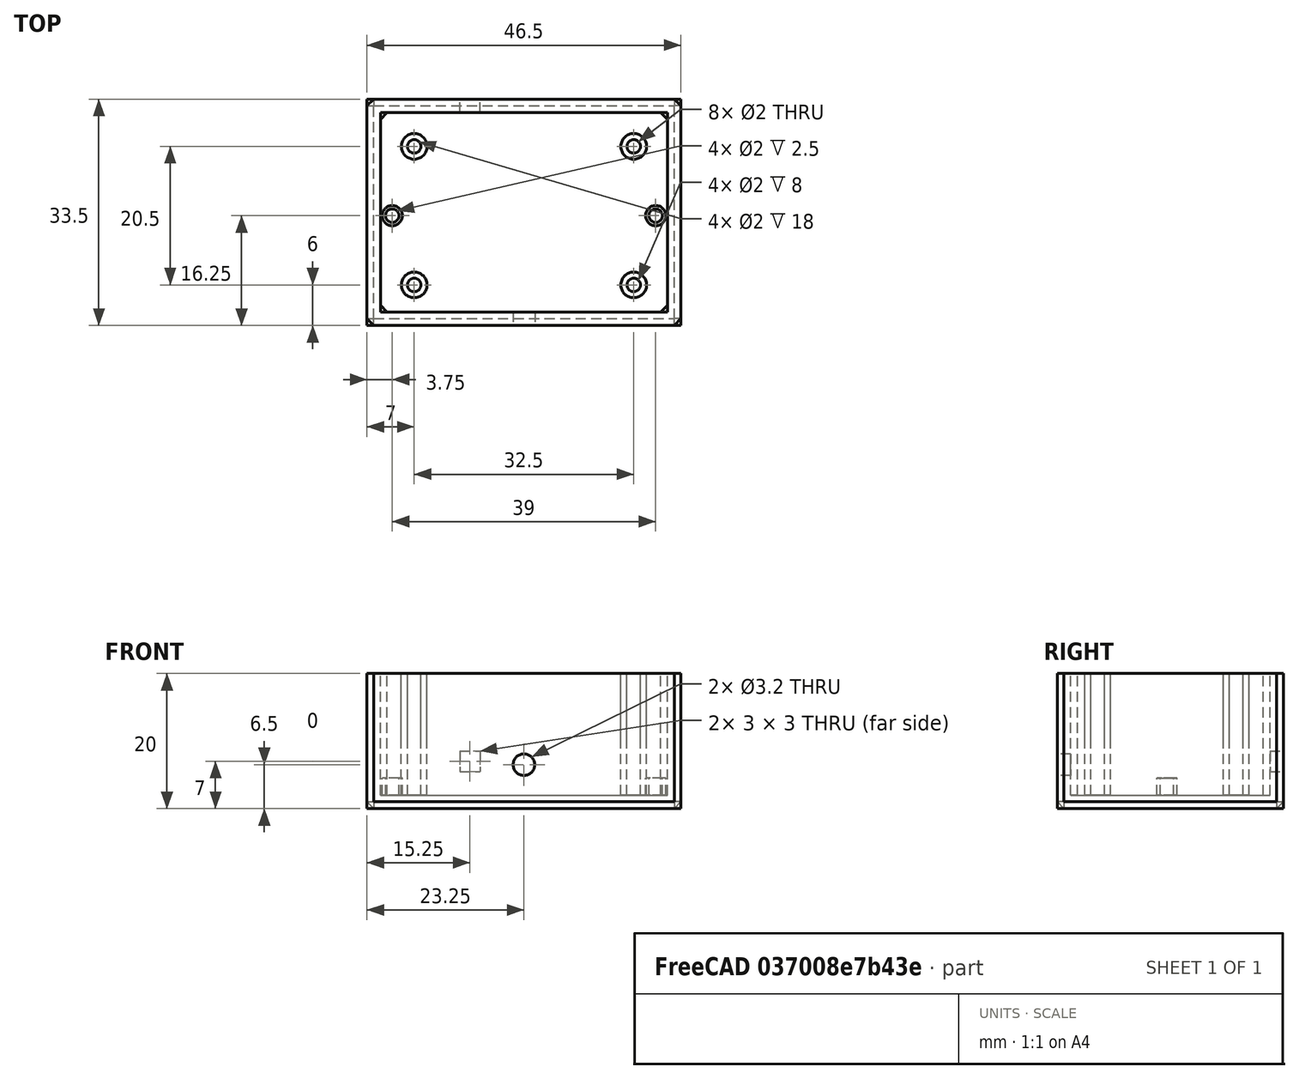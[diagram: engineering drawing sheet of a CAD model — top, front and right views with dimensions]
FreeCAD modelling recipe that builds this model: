
FCSTD DOCUMENT  (FreeCAD 0.18R16146 (Git))
Label: dog-traning-colar
License: All rights reserved
LicenseURL: http://en.wikipedia.org/wiki/All_rights_reserved
objects: Part::Cylinder×13, Part::Box×6, Part::MultiFuse×5, Part::Cut×4, Part::Feature×2, Part::Chamfer×2
note: 32 computed .brp shape members not serialized (recipe doc carries the construction recipe); baked Part::Feature solids carry a one-line shape summary decoded from their .brp

FEATURE [Part::Cylinder] Cylinder
  Angle = 360
  AttacherType = Attacher::AttachEngine3D
  Height = 10
  Radius = 1.9
FEATURE [Part::Cylinder] Cylinder001
  Angle = 360
  AttacherType = Attacher::AttachEngine3D
  Height = 10
  Placement = pos=(32.5,0,0) rot=(0,0,1;0rad)
  Radius = 1.9
FEATURE [Part::Cylinder] Cylinder002
  Angle = 360
  AttacherType = Attacher::AttachEngine3D
  Height = 10
  Placement = pos=(32.5,-20.5,0) rot=(0,0,1;0rad)
  Radius = 1.9
FEATURE [Part::Cylinder] Cylinder003
  Angle = 360
  AttacherType = Attacher::AttachEngine3D
  Height = 10
  Placement = pos=(0,-20.5,0) rot=(0,0,1;0rad)
  Radius = 1.9
FEATURE [Part::Cylinder] Cylinder004
  Angle = 360
  AttacherType = Attacher::AttachEngine3D
  Height = 10
  Placement = pos=(0,-20.5,0) rot=(0,0,1;0rad)
  Radius = 1
FEATURE [Part::Cylinder] Cylinder005
  Angle = 360
  AttacherType = Attacher::AttachEngine3D
  Height = 10
  Placement = pos=(32.5,-20.5,0) rot=(0,0,1;0rad)
  Radius = 1
FEATURE [Part::Cylinder] Cylinder006
  Angle = 360
  AttacherType = Attacher::AttachEngine3D
  Height = 10
  Placement = pos=(32.5,0,0) rot=(0,0,1;0rad)
  Radius = 1
FEATURE [Part::Cylinder] Cylinder007
  Angle = 360
  AttacherType = Attacher::AttachEngine3D
  Height = 10
  Radius = 1
FEATURE [Part::Cylinder] Cylinder008
  Angle = 360
  AttacherType = Attacher::AttachEngine3D
  Height = 2.5
  Placement = pos=(-19.5,0,0) rot=(0,0,1;0rad)
  Radius = 1.5
FEATURE [Part::Cylinder] Cylinder009
  Angle = 360
  AttacherType = Attacher::AttachEngine3D
  Height = 2.5
  Placement = pos=(19.5,0,0) rot=(0,0,1;0rad)
  Radius = 1.5
FEATURE [Part::Cylinder] Cylinder010
  Angle = 360
  AttacherType = Attacher::AttachEngine3D
  Height = 2.5
  Placement = pos=(19.5,0,0) rot=(0,0,1;0rad)
  Radius = 1
FEATURE [Part::Cylinder] Cylinder011
  Angle = 360
  AttacherType = Attacher::AttachEngine3D
  Height = 2.5
  Placement = pos=(-19.5,0,0) rot=(0,0,1;0rad)
  Radius = 1
FEATURE [Part::Box] Box  label="Cube"
  AttacherType = Attacher::AttachEngine3D
  Height = 2
  Length = 42.5
  Placement = pos=(-21.25,-14.25,-2) rot=(0,0,1;0rad)
  Width = 29.5
FEATURE [Part::MultiFuse] Fusion
  Shapes = -> [Cylinder007,Cylinder006,Cylinder005,Cylinder004]
FEATURE [Part::MultiFuse] Fusion004
  Shapes = -> [Cylinder002,Cylinder001,Cylinder,Cylinder003]
FEATURE [Part::Cut] Cut
  Base = -> Fusion004
  Placement = pos=(-16.25,10.25,0) rot=(0,0,1;0rad)
  Tool = -> Fusion
FEATURE [Part::MultiFuse] Fusion005
  Shapes = -> [Cylinder010,Cylinder011]
FEATURE [Part::MultiFuse] Fusion006
  Shapes = -> [Cylinder008,Cylinder009]
FEATURE [Part::Cut] Cut001
  Base = -> Fusion006
  Tool = -> Fusion005
FEATURE [Part::Cylinder] Cylinder012
  Angle = 360
  AttacherType = Attacher::AttachEngine3D
  Height = 10
  Placement = pos=(0,-10,4.5) rot=(1,0,0;1.5708rad)
  Radius = 1.6
FEATURE [Part::Box] Box001  label="Cube001"
  AttacherType = Attacher::AttachEngine3D
  Height = 20
  Length = 46.5
  Placement = pos=(-23.25,-16.25,-2) rot=(0,0,1;0rad)
  Width = 2
FEATURE [Part::Feature] Cut002
  Placement = pos=(-16.25,10.25,8) rot=(0,0,1;0rad)
  shape: bbox 36.3 x 24.3 x 10 mm, 16 faces, 4 solids (baked)
FEATURE [Part::Box] Box002  label="Cube002"
  AttacherType = Attacher::AttachEngine3D
  Height = 20
  Length = 46.5
  Placement = pos=(-23.25,15.25,-2) rot=(0,0,1;0rad)
  Width = 2
FEATURE [Part::Box] Box003  label="Cube003"
  AttacherType = Attacher::AttachEngine3D
  Height = 20
  Length = 2
  Placement = pos=(-23.25,-14.25,-2) rot=(0,0,1;0rad)
  Width = 29.5
FEATURE [Part::Box] Box004  label="Cube004"
  AttacherType = Attacher::AttachEngine3D
  Height = 20
  Length = 2
  Placement = pos=(21.25,-14.25,-2) rot=(0,0,1;0rad)
  Width = 29.5
FEATURE [Part::Cut] Cut003
  Base = -> Box001
  Tool = -> Cylinder012
FEATURE [Part::Box] Box005  label="Cube005"
  AttacherType = Attacher::AttachEngine3D
  Height = 3
  Length = 3
  Placement = pos=(-9.5,12,3.5) rot=(0,0,1;0rad)
  Width = 8
FEATURE [Part::Cut] Cut004
  Base = -> Box002
  Tool = -> Box005
FEATURE [Part::MultiFuse] Fusion007
  Shapes = -> [Cut004,Cut003,Box004,Box003,Cut002,Cut001,Cut,Box]
FEATURE [Part::Feature] Fusion007001  label="Fusion008"
  shape: bbox 46.5 x 33.5 x 20 mm, 40 faces (baked)
FEATURE [Part::Chamfer] Chamfer
  Base = -> Fusion007001
  Edges = 8 edges r=1: [Edge58,Edge59,Edge60,Edge62,Edge63,Edge64,Edge74,Edge75]
FEATURE [Part::Chamfer] Chamfer001
  Base = -> Chamfer
  Edges = 4 edges r=1: [Edge39,Edge40,Edge43,Edge44]
